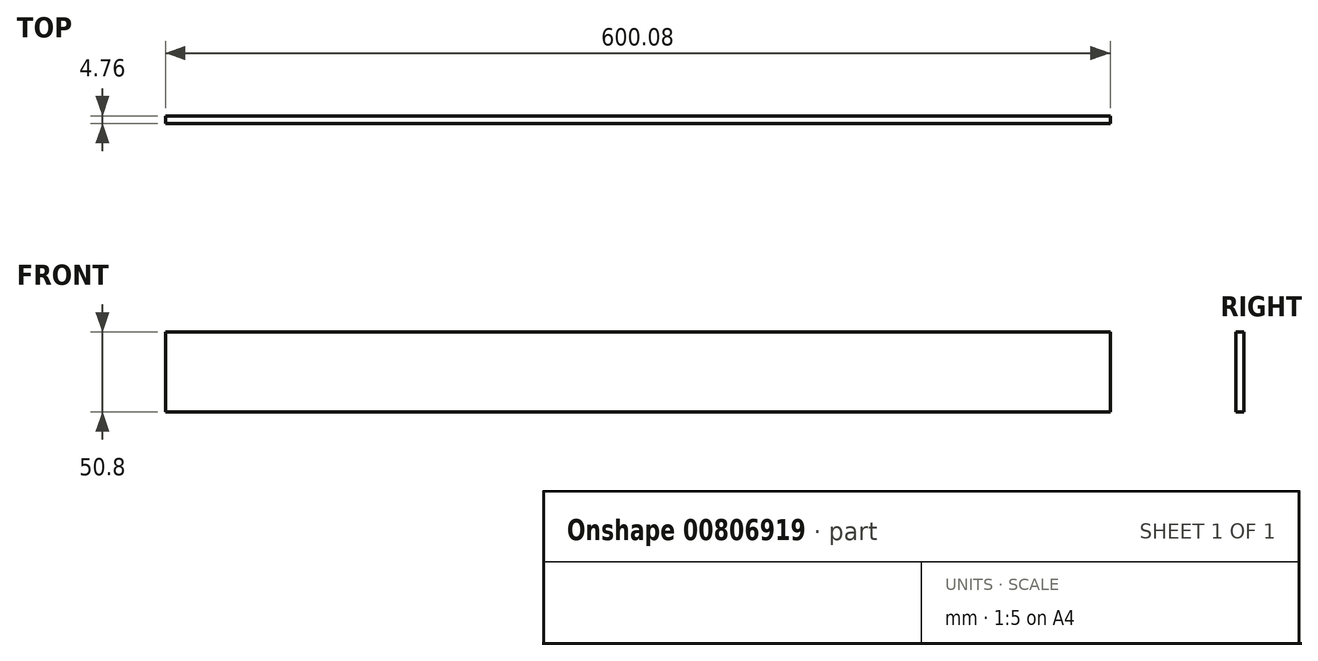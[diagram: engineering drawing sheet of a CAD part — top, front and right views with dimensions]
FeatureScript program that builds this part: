
annotation { "Feature Type Name" : "Feature", "Feature Type Description" : "" }
export const myFeature = defineFeature(function(context is Context, id is Id, definition is map)
    precondition{}
    {
        {
            var Q0;
            Q0=qCreatedBy(makeId("Top.planeOp"),FACE);
            var sketch = newSketch(context, id + "F0", { "sketchPlane" : qUnion([Q0])});
            skLineSegment(sketch, "E0", {"start": v(0, 4.76) * mm, "end": v(600.08, 4.76) * mm});
            skLineSegment(sketch, "E1", {"start": v(0, 0) * mm, "end": v(0, 4.76) * mm});
            skLineSegment(sketch, "E2", {"start": v(600.08, 0) * mm, "end": v(600.08, 4.76) * mm});
            skLineSegment(sketch, "E3", {"start": v(600.08, 0) * mm, "end": v(0, 0) * mm});
            skSolve(sketch);
        }
        {
            var Q0;
            Q0 = qSketchRegion(id + "F0", true);
            extrude(context, id + "F1", {"entities" : qUnion([Q0]), "depth" : 50.8 * mm, "offsetDistance" : 25.4 * mm});
        }
    });
